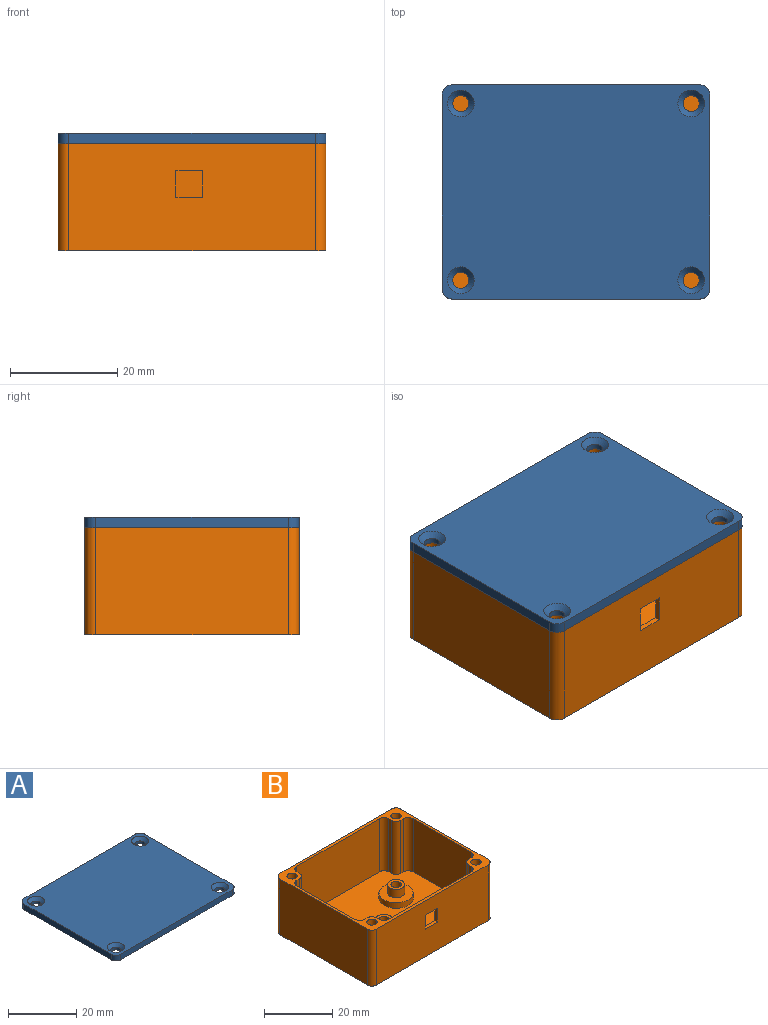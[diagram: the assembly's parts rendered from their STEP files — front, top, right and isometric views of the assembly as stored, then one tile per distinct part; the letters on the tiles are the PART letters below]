
ASSEMBLY  parts=2 mates=1
PART A: 18 faces, bbox 50x40x2 mm
  f0: plane 46x2mm, normal (0,1,0), area 92mm2, adj f4,f5,f14,f17
  f1: plane 36x2mm, normal (-1,0,0), area 72mm2, adj f4,f5,f14,f15
  f2: plane 46x2mm, normal (0,-1,0), area 92mm2, adj f4,f5,f15,f16
  f3: plane 36x2mm, normal (1,0,0), area 72mm2, adj f4,f5,f16,f17
  f4: plane 50x40mm, normal (0,0,1), area 1918mm2, adj f0,f1,f2,f3,f10,f11,f12,f13
  f5: plane 50x40mm, normal (0,0,-1), area 1968.3mm2, adj f0,f1,f2,f3,f6,f7,f8,f9
  f6: cylinder r=1.5mm len=3mm, axis (0,0,1), area 9.4mm2, adj f5,f13
  f7: cylinder r=1.5mm len=3mm, axis (0,0,1), area 9.4mm2, adj f5,f12
  f8: cylinder r=1.5mm len=3mm, axis (0,0,1), area 9.4mm2, adj f5,f11
  f9: cylinder r=1.5mm len=3mm, axis (0,0,1), area 9.4mm2, adj f5,f10
  f10: cone r=1.5mm half-angle=45deg, axis (0,0,1), area 17.8mm2, adj f4,f9
  f11: cone r=1.5mm half-angle=45deg, axis (0,0,1), area 17.8mm2, adj f4,f8
  f12: cone r=1.5mm half-angle=45deg, axis (0,0,1), area 17.8mm2, adj f4,f7
  f13: cone r=1.5mm half-angle=45deg, axis (0,0,1), area 17.8mm2, adj f4,f6
  f14: cylinder r=2mm len=2mm, axis (0,0,1), area 6.3mm2, adj f0,f1,f4,f5
  f15: cylinder r=2mm len=2mm, axis (0,0,-1), area 6.3mm2, adj f1,f2,f4,f5
  f16: cylinder r=2mm len=2mm, axis (0,0,1), area 6.3mm2, adj f2,f3,f4,f5
  f17: cylinder r=2mm len=2mm, axis (0,0,-1), area 6.3mm2, adj f0,f3,f4,f5
PART B: 71 faces, bbox 50x40x20 mm
  f0: plane 34x19mm, normal (0,1,0), area 621mm2, adj f4,f8,f55,f65,f67,f68,f69,f70
  f1: plane 46x20mm, normal (0,-1,0), area 895mm2, adj f8,f12,f52,f53,f67,f68,f69,f70
  f2: cylinder r=1.5mm len=4mm, axis (0,0,-1), area 37.7mm2, adj f30,f50
  f3: cylinder r=1.5mm len=4mm, axis (0,0,-1), area 37.7mm2, adj f32,f43
  f4: plane 48x38mm, normal (0,0,1), area 1563.5mm2, adj f0,f5,f6,f7,f13,f14,f15,f16
  f5: plane 24x19mm, normal (1,0,0), area 456mm2, adj f4,f8,f61,f66
  f6: plane 24x19mm, normal (-1,0,0), area 456mm2, adj f4,f8,f57,f60
  f7: plane 34x19mm, normal (0,-1,0), area 646mm2, adj f4,f8,f59,f63
  f8: plane 50x40mm, normal (0,0,1), area 247.7mm2, adj f0,f1,f5,f6,f7,f9,f10,f11
  f9: plane 46x20mm, normal (0,1,0), area 920mm2, adj f8,f12,f51,f54
  f10: plane 36x20mm, normal (-1,0,0), area 720mm2, adj f8,f12,f51,f52
  f11: plane 36x20mm, normal (1,0,0), area 720mm2, adj f8,f12,f53,f54
  f12: plane 50x40mm, normal (0,0,-1), area 1928.5mm2, adj f1,f9,f10,f11,f37,f38,f39,f40
  f13: plane 19x1mm, normal (0,-1,0), area 19mm2, adj f4,f8,f61,f62
  f14: plane 19x1mm, normal (1,0,0), area 19mm2, adj f4,f8,f62,f63
  f15: plane 19x1mm, normal (0,-1,0), area 19mm2, adj f4,f8,f58,f60
  f16: plane 19x1mm, normal (-1,0,0), area 19mm2, adj f4,f8,f58,f59
  f17: plane 19x1mm, normal (0,1,0), area 19mm2, adj f4,f8,f56,f57
  f18: plane 19x1mm, normal (-1,0,0), area 19mm2, adj f4,f8,f55,f56
  f19: plane 19x1mm, normal (0,1,0), area 19mm2, adj f4,f8,f64,f66
  f20: plane 19x1mm, normal (1,0,0), area 19mm2, adj f4,f8,f64,f65
  f21: cylinder r=1.5mm len=10mm, axis (0,0,1), area 94.2mm2, adj f8,f22
  f22: plane 3x3mm, normal (0,0,1), area 7.1mm2, adj f21
  f23: cylinder r=1.5mm len=10mm, axis (0,0,1), area 94.2mm2, adj f8,f24
  f24: plane 3x3mm, normal (0,0,1), area 7.1mm2, adj f23
  f25: cylinder r=1.5mm len=10mm, axis (0,0,1), area 94.2mm2, adj f8,f26
  f26: plane 3x3mm, normal (0,0,1), area 7.1mm2, adj f25
  f27: cylinder r=1.5mm len=10mm, axis (0,0,1), area 94.2mm2, adj f8,f28
  f28: plane 3x3mm, normal (0,0,1), area 7.1mm2, adj f27
  f29: cylinder r=2.5mm len=5mm, axis (0,0,-1), area 47.1mm2, adj f30,f34
  f30: plane 5x5mm, normal (0,0,1), area 12.6mm2, adj f2,f29
  f31: cylinder r=2.5mm len=5mm, axis (0,0,-1), area 47.1mm2, adj f32,f36
  f32: plane 5x5mm, normal (0,0,1), area 12.6mm2, adj f3,f31
  f33: cylinder r=5mm len=10mm, axis (0,0,-1), area 62.8mm2, adj f4,f34
  f34: plane 10x10mm, normal (0,0,1), area 58.9mm2, adj f29,f33
  f35: cylinder r=5mm len=10mm, axis (0,0,-1), area 62.8mm2, adj f4,f36
  f36: plane 10x10mm, normal (0,0,1), area 58.9mm2, adj f31,f35
  f37: plane 3.19x2mm, normal (1,0,0), area 6.4mm2, adj f12,f38,f42,f43
  f38: plane 2.77x2mm, normal (0.5,-0.87,0), area 6.4mm2, adj f12,f37,f39,f43
  f39: plane 2.77x2mm, normal (-0.5,-0.87,0), area 6.4mm2, adj f12,f38,f40,f43
  f40: plane 3.19x2mm, normal (-1,0,0), area 6.4mm2, adj f12,f39,f41,f43
  f41: plane 2.77x2mm, normal (-0.5,0.87,0), area 6.4mm2, adj f12,f40,f42,f43
  f42: plane 2.77x2mm, normal (0.5,0.87,0), area 6.4mm2, adj f12,f37,f41,f43
  f43: plane 6.39x5.53mm, normal (0,0,-1), area 19.4mm2, adj f3,f37,f38,f39,f40,f41,f42
  f44: plane 4x2mm, normal (1,0,0), area 8mm2, adj f12,f45,f49,f50
  f45: plane 3.46x2mm, normal (0.5,-0.87,0), area 8mm2, adj f12,f44,f46,f50
  f46: plane 3.46x2mm, normal (-0.5,-0.87,0), area 8mm2, adj f12,f45,f47,f50
  f47: plane 4x2mm, normal (-1,0,0), area 8mm2, adj f12,f46,f48,f50
  f48: plane 3.46x2mm, normal (-0.5,0.87,0), area 8mm2, adj f12,f47,f49,f50
  f49: plane 3.46x2mm, normal (0.5,0.87,0), area 8mm2, adj f12,f44,f48,f50
  f50: plane 8x6.93mm, normal (0,0,-1), area 34.5mm2, adj f2,f44,f45,f46,f47,f48,f49
  f51: cylinder r=2mm len=20mm, axis (0,0,1), area 62.8mm2, adj f8,f9,f10,f12
  f52: cylinder r=2mm len=20mm, axis (0,0,-1), area 62.8mm2, adj f1,f8,f10,f12
  f53: cylinder r=2mm len=20mm, axis (0,0,1), area 62.8mm2, adj f1,f8,f11,f12
  f54: cylinder r=2mm len=20mm, axis (0,0,-1), area 62.8mm2, adj f8,f9,f11,f12
  f55: cylinder r=2mm len=19mm, axis (0,0,-1), area 59.7mm2, adj f0,f4,f8,f18
  f56: cylinder r=2mm len=19mm, axis (0,0,1), area 59.7mm2, adj f4,f8,f17,f18
  f57: cylinder r=2mm len=19mm, axis (0,0,1), area 59.7mm2, adj f4,f6,f8,f17
  f58: cylinder r=2mm len=19mm, axis (0,0,1), area 59.7mm2, adj f4,f8,f15,f16
  f59: cylinder r=2mm len=19mm, axis (0,0,-1), area 59.7mm2, adj f4,f7,f8,f16
  f60: cylinder r=2mm len=19mm, axis (0,0,-1), area 59.7mm2, adj f4,f6,f8,f15
  f61: cylinder r=2mm len=19mm, axis (0,0,-1), area 59.7mm2, adj f4,f5,f8,f13
  f62: cylinder r=2mm len=19mm, axis (0,0,1), area 59.7mm2, adj f4,f8,f13,f14
  f63: cylinder r=2mm len=19mm, axis (0,0,1), area 59.7mm2, adj f4,f7,f8,f14
  f64: cylinder r=2mm len=19mm, axis (0,0,1), area 59.7mm2, adj f4,f8,f19,f20
  f65: cylinder r=2mm len=19mm, axis (0,0,1), area 59.7mm2, adj f0,f4,f8,f20
  f66: cylinder r=2mm len=19mm, axis (0,0,1), area 59.7mm2, adj f4,f5,f8,f19
  f67: plane 5x1mm, normal (0,0,-1), area 5mm2, adj f0,f1,f68,f70
  f68: plane 5x1mm, normal (1,0,0), area 5mm2, adj f0,f1,f67,f69
  f69: plane 5x1mm, normal (0,0,1), area 5mm2, adj f0,f1,f68,f70
  f70: plane 5x1mm, normal (-1,0,0), area 5mm2, adj f0,f1,f67,f69
PLACE A t=(-68,2.31,20)mm
PLACE B at identity fixed
MATE slider B.f27 <-> A.f8  axis (0,0,1) through (-16.89,25.72,20)mm
